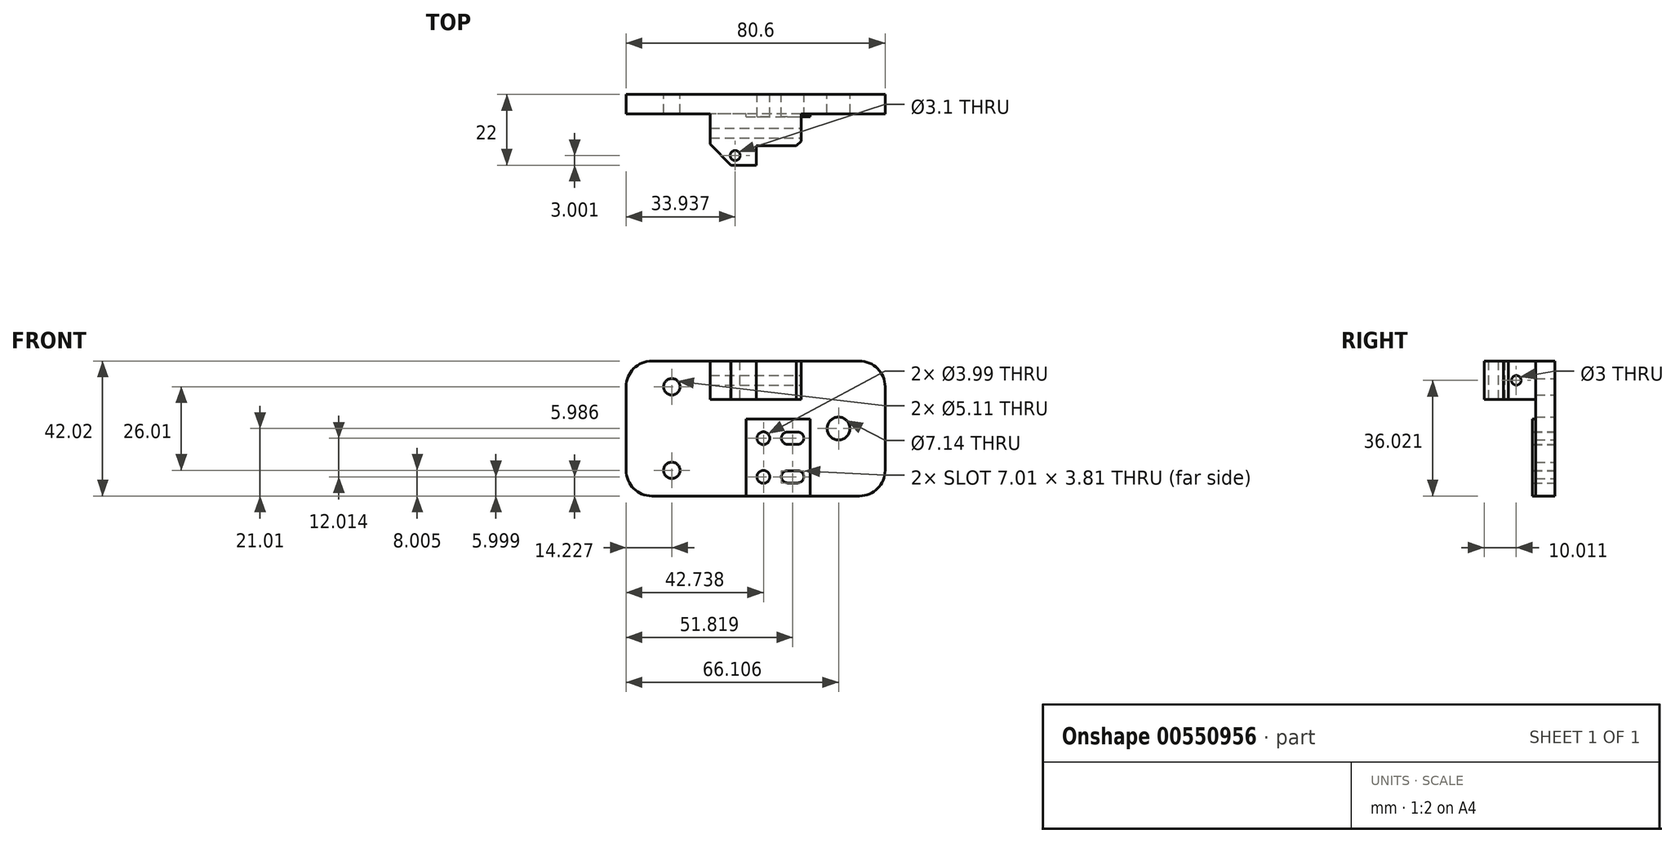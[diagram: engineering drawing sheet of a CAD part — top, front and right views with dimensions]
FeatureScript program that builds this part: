
annotation { "Feature Type Name" : "Feature", "Feature Type Description" : "" }
export const myFeature = defineFeature(function(context is Context, id is Id, definition is map)
    precondition{}
    {
        {
            var Q0;
            Q0=qCreatedBy(makeId("Front.planeOp"),FACE);
            var sketch = newSketch(context, id + "F0", { "sketchPlane" : qUnion([Q0])});
            skLineSegment(sketch, "E0.bottom", {"start": v(32.3, 21) * mm, "end": v(-32.3, 21) * mm});
            skLineSegment(sketch, "E0.top", {"start": v(32.3, -21) * mm, "end": v(-32.3, -21) * mm});
            skLineSegment(sketch, "E0.left", {"start": v(40.3, 13) * mm, "end": v(40.3, -13) * mm});
            skLineSegment(sketch, "E0.right", {"start": v(-40.3, 13) * mm, "end": v(-40.3, -13) * mm});
            skPoint(sketch, "E0.middle", {"position": v(0, 0) * mm});
            skPoint(sketch, "E1.visualSharp", {"position": v(-40.3, 21) * mm});
            skArc(sketch, "E1.filletArc", {"start": v(-32.3, 21) * mm, "mid": v(-37.95, 18.66) * mm, "end": v(-40.3, 13) * mm});
            skPoint(sketch, "E2.visualSharp", {"position": v(-40.3, -21) * mm});
            skArc(sketch, "E2.filletArc", {"start": v(-40.3, -13) * mm, "mid": v(-37.95, -18.66) * mm, "end": v(-32.3, -21) * mm});
            skPoint(sketch, "E3.visualSharp", {"position": v(40.3, -21) * mm});
            skArc(sketch, "E3.filletArc", {"start": v(32.3, -21) * mm, "mid": v(37.95, -18.66) * mm, "end": v(40.3, -13) * mm});
            skPoint(sketch, "E4.visualSharp", {"position": v(40.3, 21) * mm});
            skArc(sketch, "E4.filletArc", {"start": v(40.3, 13) * mm, "mid": v(37.95, 18.66) * mm, "end": v(32.3, 21) * mm});
            skCircle(sketch, "E5", {"center": v(25.8, 0) * mm, "radius": 3.57 * mm});
            skPoint(sketch, "E5.centerSnap0", {"position": v(40.3, 0) * mm});
            skLineSegment(sketch, "E6", {"start": v(9.92, -3) * mm, "end": v(13.12, -3) * mm});
            skArc(sketch, "E7.0.startCap", {"start": v(9.92, -4.9) * mm, "mid": v(8.01, -3) * mm, "end": v(9.92, -1.1) * mm});
            skArc(sketch, "E7.0.endCap", {"start": v(13.12, -1.1) * mm, "mid": v(15.02, -3) * mm, "end": v(13.12, -4.9) * mm});
            skLineSegment(sketch, "E7.0.left", {"start": v(9.92, -1.1) * mm, "end": v(13.12, -1.1) * mm});
            skLineSegment(sketch, "E7.0.right", {"start": v(9.92, -4.9) * mm, "end": v(13.12, -4.9) * mm});
            skLineSegment(sketch, "E8", {"start": v(9.92, -15.01) * mm, "end": v(13.12, -15.01) * mm});
            skArc(sketch, "E9.0.startCap", {"start": v(9.92, -16.92) * mm, "mid": v(8.01, -15.01) * mm, "end": v(9.92, -13.1) * mm});
            skArc(sketch, "E9.0.endCap", {"start": v(13.12, -13.1) * mm, "mid": v(15.02, -15.01) * mm, "end": v(13.12, -16.92) * mm});
            skLineSegment(sketch, "E9.0.left", {"start": v(9.92, -13.1) * mm, "end": v(13.12, -13.1) * mm});
            skLineSegment(sketch, "E9.0.right", {"start": v(9.92, -16.92) * mm, "end": v(13.12, -16.92) * mm});
            skCircle(sketch, "E10", {"center": v(2.44, -15.02) * mm, "radius": 2 * mm});
            skCircle(sketch, "E11", {"center": v(2.44, -3) * mm, "radius": 2 * mm});
            skCircle(sketch, "E12", {"center": v(-26.07, 13) * mm, "radius": 2.55 * mm});
            skCircle(sketch, "E13", {"center": v(-26.07, -13) * mm, "radius": 2.55 * mm});
            skSolve(sketch);
        }
        {
            var Q0;
            Q0 = qSketchRegion(id + "F0", true);
            extrude(context, id + "F1", {"entities" : qUnion([Q0]), "depth" : 6 * mm, "offsetDistance" : 25.4 * mm});
        }
        {
            var Q0;
            Q0=qCreatedBy(makeId("Front.planeOp"),FACE);
            var sketch = newSketch(context, id + "F2", { "sketchPlane" : qUnion([Q0])});
            skLineSegment(sketch, "E14.bottom", {"start": v(-3, -21) * mm, "end": v(16.98, -21) * mm});
            skLineSegment(sketch, "E14.top", {"start": v(-3, 3) * mm, "end": v(16.98, 3) * mm});
            skLineSegment(sketch, "E14.left", {"start": v(-3, -21) * mm, "end": v(-3, 3) * mm});
            skLineSegment(sketch, "E14.right", {"start": v(16.98, -21) * mm, "end": v(16.98, 3) * mm});
            skPoint(sketch, "E14.middle", {"position": v(6.98, -9) * mm});
            skLineSegment(sketch, "E15", {"start": v(9.92, -15.01) * mm, "end": v(13.12, -15.01) * mm});
            skCircle(sketch, "E16", {"center": v(2.44, -3) * mm, "radius": 2 * mm});
            skCircle(sketch, "E17", {"center": v(2.44, -15.02) * mm, "radius": 2 * mm});
            skArc(sketch, "E18.0.startCap", {"start": v(9.92, -16.92) * mm, "mid": v(8.01, -15.01) * mm, "end": v(9.92, -13.1) * mm});
            skArc(sketch, "E18.0.endCap", {"start": v(13.12, -13.1) * mm, "mid": v(15.02, -15.01) * mm, "end": v(13.12, -16.92) * mm});
            skLineSegment(sketch, "E18.0.left", {"start": v(9.92, -13.1) * mm, "end": v(13.12, -13.1) * mm});
            skLineSegment(sketch, "E18.0.right", {"start": v(9.92, -16.92) * mm, "end": v(13.12, -16.92) * mm});
            skArc(sketch, "E19.0.startCap", {"start": v(9.92, -4.9) * mm, "mid": v(8.01, -3) * mm, "end": v(9.92, -1.1) * mm});
            skArc(sketch, "E19.0.endCap", {"start": v(13.12, -1.1) * mm, "mid": v(15.02, -3) * mm, "end": v(13.12, -4.9) * mm});
            skLineSegment(sketch, "E19.0.left", {"start": v(9.92, -1.1) * mm, "end": v(13.12, -1.1) * mm});
            skLineSegment(sketch, "E19.0.right", {"start": v(9.92, -4.9) * mm, "end": v(13.12, -4.9) * mm});
            skSolve(sketch);
        }
        {
            var Q0;
            Q0 = qSketchRegion(id + "F2", true);
            extrude(context, id + "F3", {"entities" : qUnion([Q0]), "operationType" : NewBodyOperationType.ADD, "depth" : 7 * mm, "offsetDistance" : 25.4 * mm});
        }
        {
            var Q0;
            Q0=makeQuery(id+"F1.opExtrude","SWEPT_FACE",FACE,{"disambiguationData":[OSD([sQuery(id+"F0.wireOp",EDGE,"E0.bottom")])]});
            var sketch = newSketch(context, id + "F4", { "sketchPlane" : qUnion([Q0])});
            skLineSegment(sketch, "E20.0", {"start": v(32.3, -6) * mm, "end": v(-32.3, -6) * mm, "construction": true});
            skLineSegment(sketch, "E21", {"start": v(-14.19, -6) * mm, "end": v(-14.19, -15.5) * mm});
            skLineSegment(sketch, "E22", {"start": v(-14.19, -15.5) * mm, "end": v(-7.68, -22) * mm});
            skLineSegment(sketch, "E23", {"start": v(-7.68, -22) * mm, "end": v(0.2, -22) * mm});
            skLineSegment(sketch, "E24", {"start": v(0.2, -22) * mm, "end": v(0.2, -16) * mm});
            skLineSegment(sketch, "E25", {"start": v(0.2, -16) * mm, "end": v(12.69, -16) * mm});
            skLineSegment(sketch, "E26", {"start": v(12.69, -16) * mm, "end": v(14.19, -14.5) * mm});
            skLineSegment(sketch, "E27", {"start": v(14.19, -14.5) * mm, "end": v(14.19, -6) * mm});
            skCircle(sketch, "E28", {"center": v(-6.36, -19) * mm, "radius": 1.55 * mm});
            skPoint(sketch, "E29.0", {"position": v(-40.3, -6) * mm});
            skLineSegment(sketch, "E30", {"start": v(-14.19, -6) * mm, "end": v(14.19, -6) * mm});
            skSolve(sketch);
        }
        {
            var Q0;
            Q0 = qSketchRegion(id + "F4", true);
            extrude(context, id + "F5", {"entities" : qUnion([Q0]), "operationType" : NewBodyOperationType.ADD, "depth" : -12 * mm, "offsetDistance" : 25.4 * mm});
        }
        {
            var Q0;
            Q0=makeQuery(id+"F5.opExtrude","SWEPT_FACE",FACE,{"disambiguationData":[OSD([sQuery(id+"F4.wireOp",EDGE,"E27")])]});
            var sketch = newSketch(context, id + "F6", { "sketchPlane" : qUnion([Q0])});
            skLineSegment(sketch, "E31.0", {"start": v(-6, 9.02) * mm, "end": v(-6, 21) * mm, "construction": true});
            skLineSegment(sketch, "E32.0", {"start": v(-14.5, 21) * mm, "end": v(-6, 21) * mm, "construction": true});
            skCircle(sketch, "E33", {"center": v(-11.99, 15.01) * mm, "radius": 1.5 * mm});
            skSolve(sketch);
        }
        {
            var Q0;
            Q0=sQuery(id+"F6.wireOp",VERTEX,"E33.center");
            var Q1;
            Q1=makeQuery(id+"F1.opExtrude","SWEPT_BODY",BODY,{"disambiguationData":[OSD([sQuery(id+"F0.wireOp",EDGE,"E0.bottom"),sQuery(id+"F0.wireOp",EDGE,"E0.top"),sQuery(id+"F0.wireOp",EDGE,"E0.left"),sQuery(id+"F0.wireOp",EDGE,"E0.right"),sQuery(id+"F0.wireOp",EDGE,"E1.filletArc"),sQuery(id+"F0.wireOp",EDGE,"E2.filletArc"),sQuery(id+"F0.wireOp",EDGE,"E3.filletArc"),sQuery(id+"F0.wireOp",EDGE,"E4.filletArc"),sQuery(id+"F0.wireOp",EDGE,"Dkx74ZR5-ZXyQ-2bw9-to7L-jgdulx6oR5GS"),sQuery(id+"F0.wireOp",EDGE,"Ns57h2T9-ZO04-R4jJ-xUDp-XpG5Lbc0IB0O"),sQuery(id+"F0.wireOp",EDGE,"E5"),sQuery(id+"F0.wireOp",EDGE,"E7.0.startCap"),sQuery(id+"F0.wireOp",EDGE,"E7.0.endCap"),sQuery(id+"F0.wireOp",EDGE,"E7.0.left"),sQuery(id+"F0.wireOp",EDGE,"E7.0.right"),sQuery(id+"F0.wireOp",EDGE,"E9.0.startCap"),sQuery(id+"F0.wireOp",EDGE,"E9.0.endCap"),sQuery(id+"F0.wireOp",EDGE,"E9.0.left"),sQuery(id+"F0.wireOp",EDGE,"E9.0.right"),sQuery(id+"F0.wireOp",EDGE,"E10"),sQuery(id+"F0.wireOp",EDGE,"E11")])]});
            hole(context, id + "F7", {"style" : HoleStyle.SIMPLE, "endStyle" : HoleEndStyle.THROUGH, "holeDiameter" : 3 * mm, "majorDiameter" : 6.35 * mm, "isTappedThrough" : true, "tappedDepth" : 12.7 * mm, "tapClearance" : 3, "locations" : qUnion([Q0]), "scope" : qUnion([Q1])});
        }
    });
